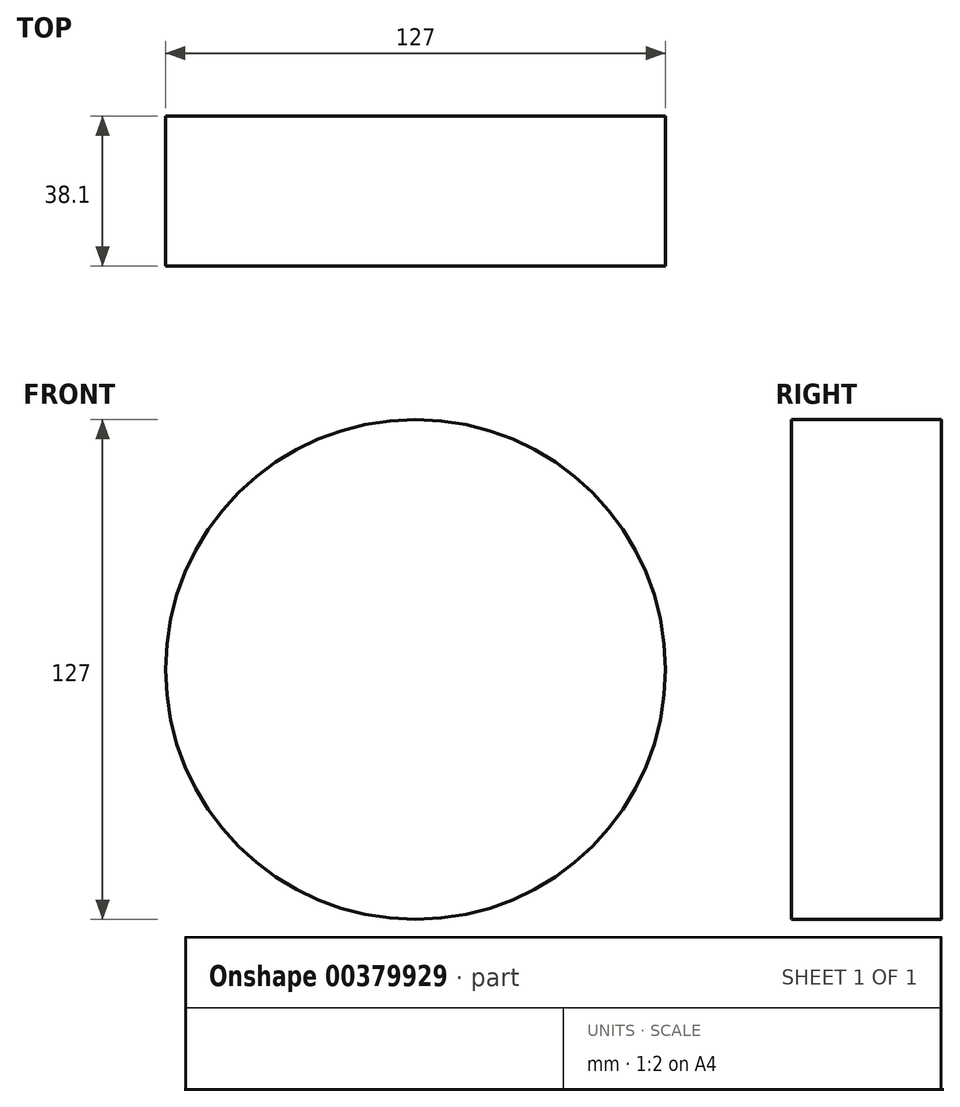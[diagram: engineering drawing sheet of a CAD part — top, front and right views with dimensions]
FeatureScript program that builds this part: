
annotation { "Feature Type Name" : "Feature", "Feature Type Description" : "" }
export const myFeature = defineFeature(function(context is Context, id is Id, definition is map)
    precondition{}
    {
        {
            var Q0;
            Q0=qCreatedBy(makeId("Front.planeOp"),FACE);
            var sketch = newSketch(context, id + "F0", { "sketchPlane" : qUnion([Q0])});
            skCircle(sketch, "E0", {"center": v(0, 0) * mm, "radius": 63.5 * mm});
            skSolve(sketch);
        }
        {
            var Q0;
            Q0=makeQuery(id+"F0.imprint","IMPRINT",FACE,{"disambiguationData":[TD([[makeQuery(id+"F0.imprint","IMPRINT",EDGE,{"derivedFrom":sQuery(id+"F0.wireOp",EDGE,"E0")}),1.0]])]});
            extrude(context, id + "F1", {"entities" : qUnion([Q0]), "depth" : 38.1 * mm});
        }
    });
